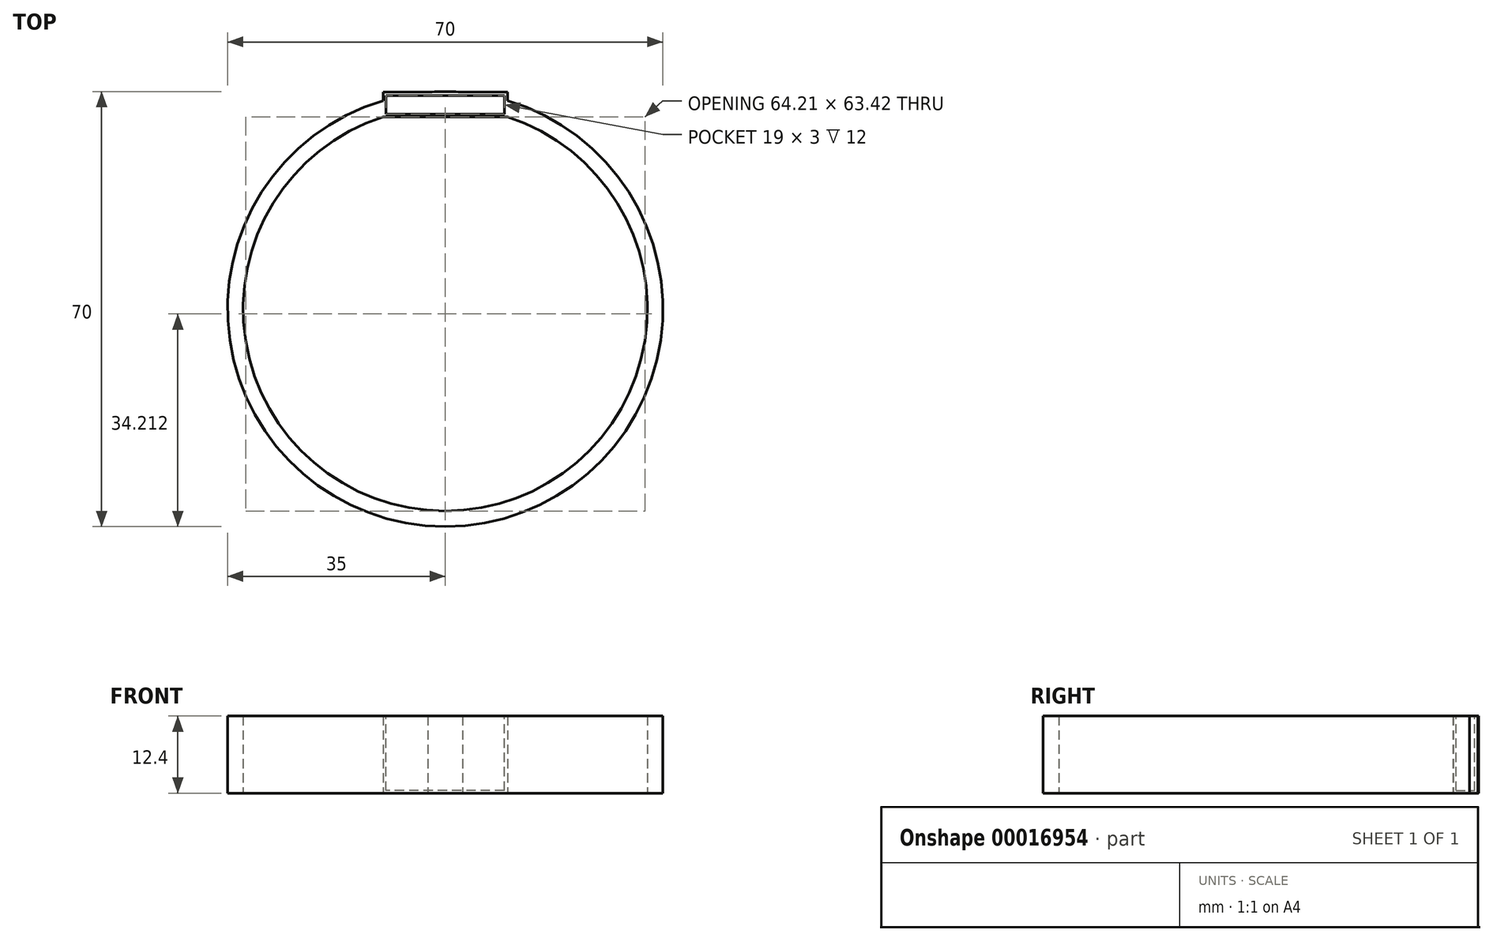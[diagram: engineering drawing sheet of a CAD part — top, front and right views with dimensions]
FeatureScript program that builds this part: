
annotation { "Feature Type Name" : "Feature", "Feature Type Description" : "" }
export const myFeature = defineFeature(function(context is Context, id is Id, definition is map)
    precondition{}
    {
        {
            var Q0;
            Q0=qCreatedBy(makeId("Top.planeOp"),FACE);
            var sketch = newSketch(context, id + "F0", { "sketchPlane" : qUnion([Q0])});
            skCircle(sketch, "E0", {"center": v(0, 0) * mm, "radius": 35 * mm});
            skCircle(sketch, "E1", {"center": v(0, 0) * mm, "radius": 32.5 * mm});
            skSolve(sketch);
        }
        {
            var Q0;
            Q0=makeQuery(id+"F0.imprint","IMPRINT",FACE,{"disambiguationData":[TD([[makeQuery(id+"F0.imprint","IMPRINT",EDGE,{"derivedFrom":sQuery(id+"F0.wireOp",EDGE,"E0")}),1.0]])]});
            extrude(context, id + "F1", {"entities" : qUnion([Q0]), "depth" : 12.4 * mm});
        }
        {
            var Q0;
            Q0=makeQuery(id+"F1.opExtrude","CAP_FACE",FACE,{"disambiguationData":[OSD([sQuery(id+"F0.wireOp",EDGE,"E0"),sQuery(id+"F0.wireOp",EDGE,"E1")])],"isStart":false});
            var sketch = newSketch(context, id + "F2", { "sketchPlane" : qUnion([Q0])});
            skSolve(sketch);
        }
        {
            var Q0;
            Q0=qCreatedBy(makeId("Top.planeOp"),FACE);
            var sketch = newSketch(context, id + "F3", { "sketchPlane" : qUnion([Q0])});
            skLineSegment(sketch, "E2.rect.bottom", {"start": v(10, 30.9) * mm, "end": v(-10, 30.9) * mm});
            skLineSegment(sketch, "E2.rect.top", {"start": v(10, 34.9) * mm, "end": v(-10, 34.9) * mm});
            skLineSegment(sketch, "E2.rect.left", {"start": v(10, 30.9) * mm, "end": v(10, 34.9) * mm});
            skLineSegment(sketch, "E2.rect.right", {"start": v(-10, 30.9) * mm, "end": v(-10, 34.9) * mm});
            skPoint(sketch, "E2.rect.middle", {"position": v(0, 32.9) * mm});
            skSolve(sketch);
        }
        {
            var Q0;
            Q0=makeQuery(id+"F3.imprint","IMPRINT",FACE,{"disambiguationData":[TD([[makeQuery(id+"F3.imprint","IMPRINT",EDGE,{"derivedFrom":sQuery(id+"F3.wireOp",EDGE,"E2.rect.bottom")}),-1.0]])]});
            extrude(context, id + "F4", {"entities" : qUnion([Q0]), "operationType" : NewBodyOperationType.ADD, "depth" : 12.4 * mm});
        }
        {
            var Q0;
            Q0=makeQuery(id+"F2.imprint","IMPRINT",FACE,{"disambiguationData":[TD([[makeQuery(id+"F2.imprint","IMPRINT",EDGE,{"derivedFrom":makeQuery(id+"F1.opExtrude","CAP_EDGE",EDGE,{"disambiguationData":[OSD([sQuery(id+"F0.wireOp",EDGE,"E0")])],"isStart":false})}),1.0]])]});
            var sketch = newSketch(context, id + "F5", { "sketchPlane" : qUnion([Q0])});
            skLineSegment(sketch, "E3.rect.bottom", {"start": v(9.5, 31.37) * mm, "end": v(-9.5, 31.37) * mm});
            skLineSegment(sketch, "E3.rect.top", {"start": v(9.5, 34.37) * mm, "end": v(-9.5, 34.37) * mm});
            skLineSegment(sketch, "E3.rect.left", {"start": v(9.5, 31.37) * mm, "end": v(9.5, 34.37) * mm});
            skLineSegment(sketch, "E3.rect.right", {"start": v(-9.5, 31.37) * mm, "end": v(-9.5, 34.37) * mm});
            skPoint(sketch, "E3.rect.middle", {"position": v(0, 32.87) * mm});
            skSolve(sketch);
        }
        {
            var Q0;
            {var subQ1=sQuery(id+"F5.wireOp",EDGE,"E3.rect.bottom");var subQ9=sQuery(id+"F5.wireOp",EDGE,"E3.rect.left");var subQ13=makeQuery(id+"F5.imprint","INTERSECT",VERTEX,{"derivedFrom":[subQ1,subQ9]});Q0=makeQuery(id+"F5.imprint","IMPRINT",FACE,{"disambiguationData":[TD([[makeQuery(id+"F5.imprint","IMPRINT",EDGE,{"disambiguationData":[TD([[subQ13,-1.0]])],"derivedFrom":subQ1}),-1.0]])]});}
            var Q1;
            {var subQ1=sQuery(id+"F5.wireOp",EDGE,"E3.rect.right");var subQ3=sQuery(id+"F5.wireOp",EDGE,"E3.rect.top");var subQ5=makeQuery(id+"F5.imprint","INTERSECT",VERTEX,{"derivedFrom":[subQ3,subQ1]});Q1=makeQuery(id+"F5.imprint","IMPRINT",FACE,{"disambiguationData":[TD([[makeQuery(id+"F5.imprint","IMPRINT",EDGE,{"disambiguationData":[TD([[subQ5,1.0]])],"derivedFrom":subQ3}),1.0]])]});}
            var Q2;
            {var subQ0=makeQuery(id+"F2.imprint","IMPRINT",EDGE,{"derivedFrom":makeQuery(id+"F1.opExtrude","CAP_EDGE",EDGE,{"disambiguationData":[OSD([sQuery(id+"F0.wireOp",EDGE,"E1")])],"isStart":false})});var subQ1=sQuery(id+"F5.wireOp",EDGE,"E3.rect.bottom");var subQ3=makeQuery(id+"F5.imprint","INTERSECT",VERTEX,{"disambiguationData":[OD(0.0)],"derivedFrom":[subQ0,subQ1]});Q2=makeQuery(id+"F5.imprint","IMPRINT",FACE,{"disambiguationData":[TD([[makeQuery(id+"F5.imprint","IMPRINT",EDGE,{"disambiguationData":[TD([[subQ3,-1.0]])],"derivedFrom":subQ1}),-1.0]])]});}
            var Q3;
            {var subQ1=sQuery(id+"F5.wireOp",EDGE,"E3.rect.left");var subQ3=sQuery(id+"F5.wireOp",EDGE,"E3.rect.top");var subQ5=makeQuery(id+"F5.imprint","INTERSECT",VERTEX,{"derivedFrom":[subQ3,subQ1]});Q3=makeQuery(id+"F5.imprint","IMPRINT",FACE,{"disambiguationData":[TD([[makeQuery(id+"F5.imprint","IMPRINT",EDGE,{"disambiguationData":[TD([[subQ5,-1.0]])],"derivedFrom":subQ3}),1.0]])]});}
            var Q4;
            Q4=sQuery(id+"F5.wireOp",EDGE,"E3.rect.bottom");
            var Q5;
            Q5=sQuery(id+"F5.wireOp",EDGE,"E3.rect.right");
            var Q6;
            Q6=sQuery(id+"F5.wireOp",EDGE,"E3.rect.top");
            var Q7;
            Q7=sQuery(id+"F5.wireOp",EDGE,"E3.rect.left");
            extrude(context, id + "F6", {"entities" : qUnion([Q0, Q1, Q2, Q3]), "operationType" : NewBodyOperationType.REMOVE, "surfaceEntities" : qUnion([Q4, Q5, Q6, Q7]), "oppositeDirection" : true, "depth" : 12 * mm});
        }
    });
